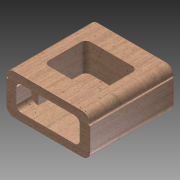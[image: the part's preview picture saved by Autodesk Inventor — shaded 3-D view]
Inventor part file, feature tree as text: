
AUTODESK INVENTOR PART (.ipt)
format: ipt  version: 2015 (Build 190159000, 159)  size: 241,152 bytes
history: native  units: in
note: dims shown in document units (in); Inventor stores cm internally (conversion verified against a paired STEP export)
features: extrude x5, sketch x5, fillet x2
ambient origin geometry x8: Origin, YZ Plane, XZ Plane, XY Plane, X Axis, Y Axis, Z Axis, Center Point
bodies: Solid1 (feature_tree)
feature tree (12):
  extrude  "Extrusion1"  Depth=1.53in
  extrude  "Extrusion2"  Depth=2.4in
  extrude  "Extrusion3"  Depth=0.57in TaperAngle=0.0deg
  extrude  "Extrusion4"  Depth=2.5in
  fillet  "Fillet1"  Radius=1.0in
  fillet  "Fillet2"  Radius=0.57in
  extrude  "Extrusion5"  Depth=0.82in
  sketch  "Sketch1"  dims[d0=3.17in d1=1.53in]
  sketch  "Sketch2"  dims[d2=3.17in d3=0.0in d4=2.4in]
  sketch  "Sketch3"  dims[d5=0.93in d7=0.57in d8=0.0in]
  sketch  "Sketch4"  dims[d9=0.2in d10=2.5in d11=1.0in d12=0.57in d13=0.0in]
  sketch  "Sketch6"  dims[d14=0.3in d15=0.82in d16=1.59in d17=1.975in d18=1.07in d19=0.0in d20=0.06in d21=0.3in d23=0.01in d26=0.65in d28=0.65in d30=0.0in d31=0.0in d32=0.75in d33=0.0in]
